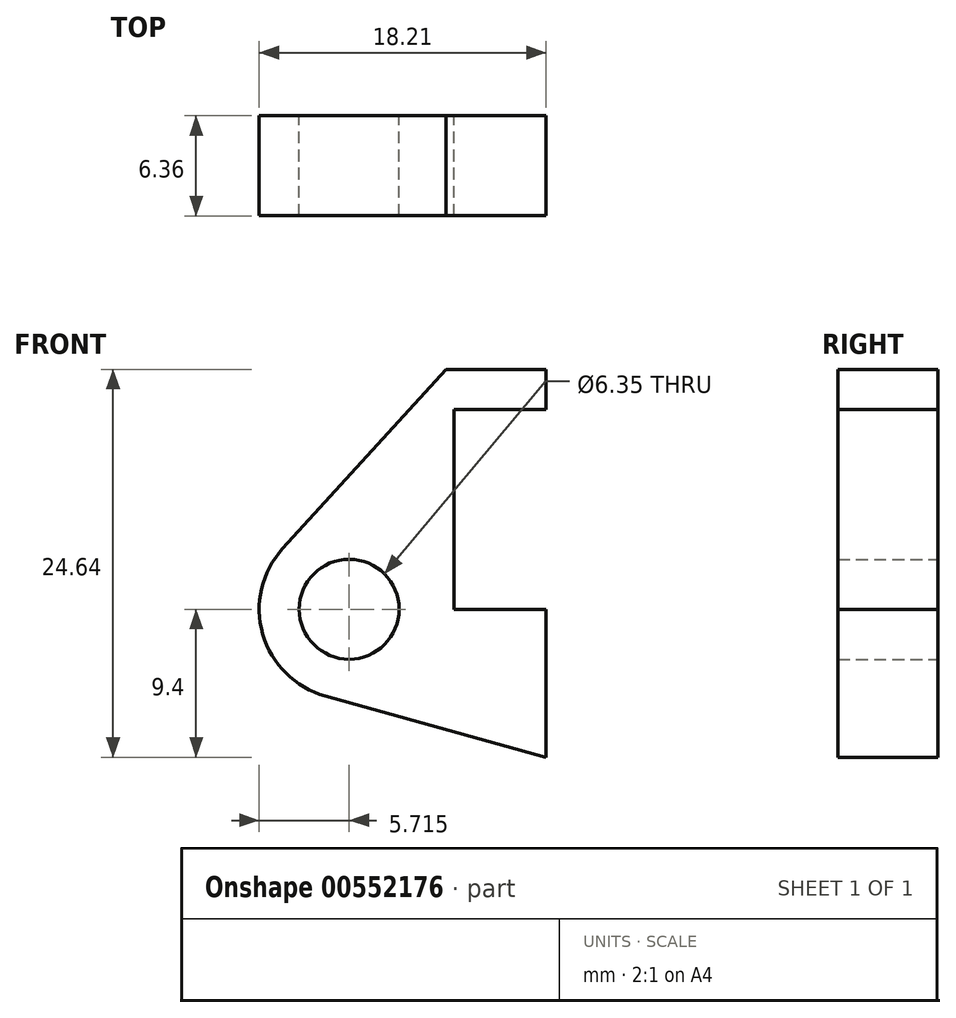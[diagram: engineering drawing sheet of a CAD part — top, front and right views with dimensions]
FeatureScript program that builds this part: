
annotation { "Feature Type Name" : "Feature", "Feature Type Description" : "" }
export const myFeature = defineFeature(function(context is Context, id is Id, definition is map)
    precondition{}
    {
        {
            var Q0;
            Q0=qCreatedBy(makeId("Front.planeOp"),FACE);
            var sketch = newSketch(context, id + "F0", { "sketchPlane" : qUnion([Q0])});
            skLineSegment(sketch, "E0", {"start": v(0, 0) * mm, "end": v(0, 12.7) * mm});
            skLineSegment(sketch, "E1", {"start": v(0, 12.7) * mm, "end": v(10.16, 12.7) * mm});
            skLineSegment(sketch, "E2", {"start": v(10.16, 12.7) * mm, "end": v(10.16, 10.16) * mm});
            skLineSegment(sketch, "E3", {"start": v(10.16, 10.16) * mm, "end": v(56.13, 10.16) * mm});
            skLineSegment(sketch, "E4", {"start": v(56.13, 10.16) * mm, "end": v(56.13, 12.7) * mm});
            skLineSegment(sketch, "E5", {"start": v(56.13, 12.7) * mm, "end": v(66.3, 12.7) * mm});
            skLineSegment(sketch, "E6", {"start": v(66.3, 12.7) * mm, "end": v(66.3, 0) * mm});
            skLineSegment(sketch, "E7", {"start": v(66.3, 0) * mm, "end": v(0, 0) * mm});
            skLineSegment(sketch, "E8", {"start": v(5.84, 15.24) * mm, "end": v(-0.5, 15.24) * mm});
            skLineSegment(sketch, "E9", {"start": v(-0.5, 15.24) * mm, "end": v(-10.88, 3.85) * mm});
            skLineSegment(sketch, "E10", {"start": v(0, 0) * mm, "end": v(-6.65, 0) * mm});
            skCircle(sketch, "E11", {"center": v(-6.65, 0) * mm, "radius": 5.72 * mm});
            skCircle(sketch, "E12", {"center": v(-6.65, 0) * mm, "radius": 3.18 * mm});
            skLineSegment(sketch, "E13", {"start": v(5.84, 15.24) * mm, "end": v(5.84, -9.4) * mm});
            skLineSegment(sketch, "E14", {"start": v(5.84, -9.4) * mm, "end": v(-8.18, -5.5) * mm});
            skSolve(sketch);
        }
        {
            var Q0;
            {var subQ1=sQuery(id+"F0.wireOp",EDGE,"E0");Q0=makeQuery(id+"F0.imprint","IMPRINT",FACE,{"disambiguationData":[TD([[makeQuery(id+"F0.imprint","IMPRINT",EDGE,{"derivedFrom":subQ1}),1.0]])]});}
            var Q1;
            {var subQ0=sQuery(id+"F0.wireOp",EDGE,"E14");Q1=makeQuery(id+"F0.imprint","IMPRINT",FACE,{"disambiguationData":[TD([[makeQuery(id+"F0.imprint","IMPRINT",EDGE,{"derivedFrom":subQ0}),-1.0]])]});}
            var Q2;
            {var subQ5=sQuery(id+"F0.wireOp",EDGE,"E12");Q2=makeQuery(id+"F0.imprint","IMPRINT",FACE,{"disambiguationData":[TD([[makeQuery(id+"F0.imprint","IMPRINT",EDGE,{"derivedFrom":subQ5}),-1.0]])]});}
            extrude(context, id + "F1", {"entities" : qUnion([Q0, Q1, Q2]), "endBound" : BoundingType.SYMMETRIC, "depth" : 6.35 * mm, "offsetDistance" : 25.4 * mm});
        }
    });
